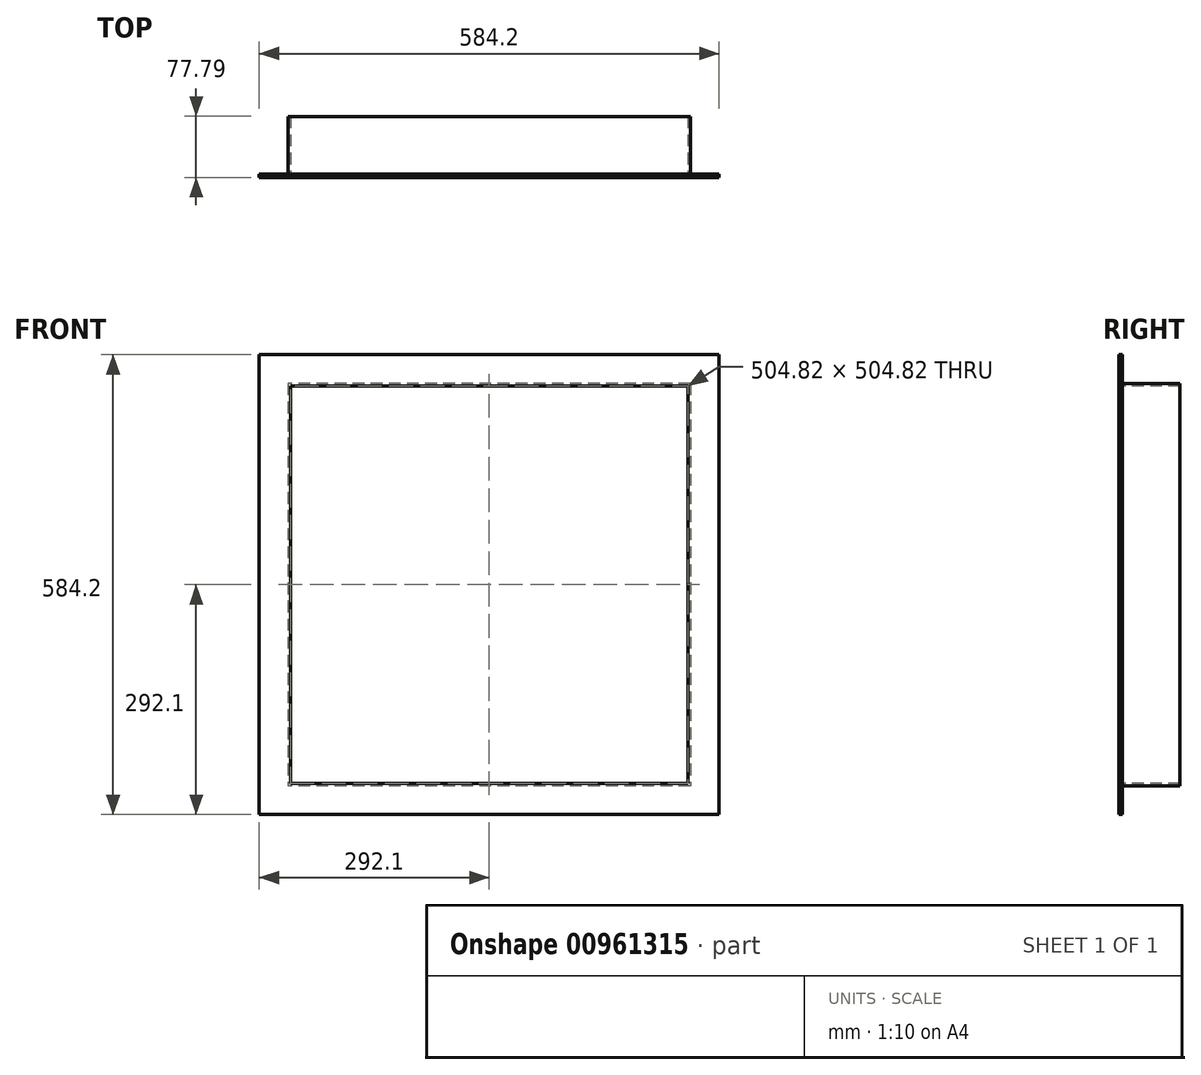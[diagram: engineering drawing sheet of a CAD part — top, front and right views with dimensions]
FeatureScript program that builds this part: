
annotation { "Feature Type Name" : "Feature", "Feature Type Description" : "" }
export const myFeature = defineFeature(function(context is Context, id is Id, definition is map)
    precondition{}
    {
        {
            var Q0;
            Q0=qCreatedBy(makeId("Front.planeOp"),FACE);
            var sketch = newSketch(context, id + "F0", { "sketchPlane" : qUnion([Q0])});
            skLineSegment(sketch, "E0.bottom", {"start": v(255.59, 255.59) * mm, "end": v(-255.59, 255.59) * mm});
            skLineSegment(sketch, "E0.top", {"start": v(255.59, -255.59) * mm, "end": v(-255.59, -255.59) * mm});
            skLineSegment(sketch, "E0.left", {"start": v(255.59, 255.59) * mm, "end": v(255.59, -255.59) * mm});
            skLineSegment(sketch, "E0.right", {"start": v(-255.59, 255.59) * mm, "end": v(-255.59, -255.59) * mm});
            skPoint(sketch, "E0.middle", {"position": v(0, 0) * mm});
            skSolve(sketch);
        }
        {
            var Q0;
            Q0=makeQuery(id+"F0.imprint","IMPRINT",FACE,{"disambiguationData":[TD([[makeQuery(id+"F0.imprint","IMPRINT",EDGE,{"derivedFrom":sQuery(id+"F0.wireOp",EDGE,"E0.bottom")}),1.0]])]});
            extrude(context, id + "F1", {"entities" : qUnion([Q0]), "oppositeDirection" : true, "depth" : 73.02 * mm, "offsetDistance" : 25.4 * mm});
        }
        {
            var Q0;
            Q0=makeQuery(id+"F1.opExtrude","CAP_FACE",FACE,{"disambiguationData":[OSD([sQuery(id+"F0.wireOp",EDGE,"E0.bottom"),sQuery(id+"F0.wireOp",EDGE,"E0.top"),sQuery(id+"F0.wireOp",EDGE,"E0.left"),sQuery(id+"F0.wireOp",EDGE,"E0.right")])],"isStart":true});
            var sketch = newSketch(context, id + "F2", { "sketchPlane" : qUnion([Q0])});
            skLineSegment(sketch, "E1.bottom", {"start": v(292.1, 292.1) * mm, "end": v(-292.1, 292.1) * mm});
            skLineSegment(sketch, "E1.top", {"start": v(292.1, -292.1) * mm, "end": v(-292.1, -292.1) * mm});
            skLineSegment(sketch, "E1.left", {"start": v(292.1, 292.1) * mm, "end": v(292.1, -292.1) * mm});
            skLineSegment(sketch, "E1.right", {"start": v(-292.1, 292.1) * mm, "end": v(-292.1, -292.1) * mm});
            skPoint(sketch, "E1.middle", {"position": v(0, 0) * mm});
            skSolve(sketch);
        }
        {
            var Q0;
            Q0=makeQuery(id+"F2.imprint","IMPRINT",FACE,{"disambiguationData":[TD([[makeQuery(id+"F2.imprint","IMPRINT",EDGE,{"derivedFrom":sQuery(id+"F2.wireOp",EDGE,"E1.bottom")}),1.0]])]});
            var Q1;
            Q1=makeQuery(id+"F2.imprint","IMPRINT",FACE,{"disambiguationData":[TD([[makeQuery(id+"F2.imprint","IMPRINT",EDGE,{"derivedFrom":makeQuery(id+"F1.opExtrude","CAP_EDGE",EDGE,{"disambiguationData":[OSD([sQuery(id+"F0.wireOp",EDGE,"E0.bottom")])],"isStart":true})}),1.0]])]});
            extrude(context, id + "F3", {"entities" : qUnion([Q0, Q1]), "operationType" : NewBodyOperationType.ADD, "depth" : 4.76 * mm, "offsetDistance" : 25.4 * mm});
        }
        {
            var Q0;
            Q0=makeQuery(id+"F3.opExtrude","CAP_FACE",FACE,{"disambiguationData":[OSD([sQuery(id+"F2.wireOp",EDGE,"E1.bottom"),sQuery(id+"F2.wireOp",EDGE,"E1.top"),sQuery(id+"F2.wireOp",EDGE,"E1.left"),sQuery(id+"F2.wireOp",EDGE,"E1.right")])],"isStart":false});
            var sketch = newSketch(context, id + "F4", { "sketchPlane" : qUnion([Q0])});
            skLineSegment(sketch, "E2.bottom", {"start": v(-252.41, -252.41) * mm, "end": v(252.41, -252.41) * mm});
            skLineSegment(sketch, "E2.top", {"start": v(-252.41, 252.41) * mm, "end": v(252.41, 252.41) * mm});
            skLineSegment(sketch, "E2.left", {"start": v(-252.41, -252.41) * mm, "end": v(-252.41, 252.41) * mm});
            skLineSegment(sketch, "E2.right", {"start": v(252.41, -252.41) * mm, "end": v(252.41, 252.41) * mm});
            skPoint(sketch, "E2.middle", {"position": v(0, 0) * mm});
            skSolve(sketch);
        }
        {
            var Q0;
            Q0=makeQuery(id+"F4.imprint","IMPRINT",FACE,{"disambiguationData":[TD([[makeQuery(id+"F4.imprint","IMPRINT",EDGE,{"derivedFrom":sQuery(id+"F4.wireOp",EDGE,"E2.bottom")}),1.0]])]});
            extrude(context, id + "F5", {"entities" : qUnion([Q0]), "operationType" : NewBodyOperationType.REMOVE, "endBound" : BoundingType.THROUGH_ALL, "oppositeDirection" : true, "depth" : 25.4 * mm, "offsetDistance" : 25.4 * mm});
        }
    });
